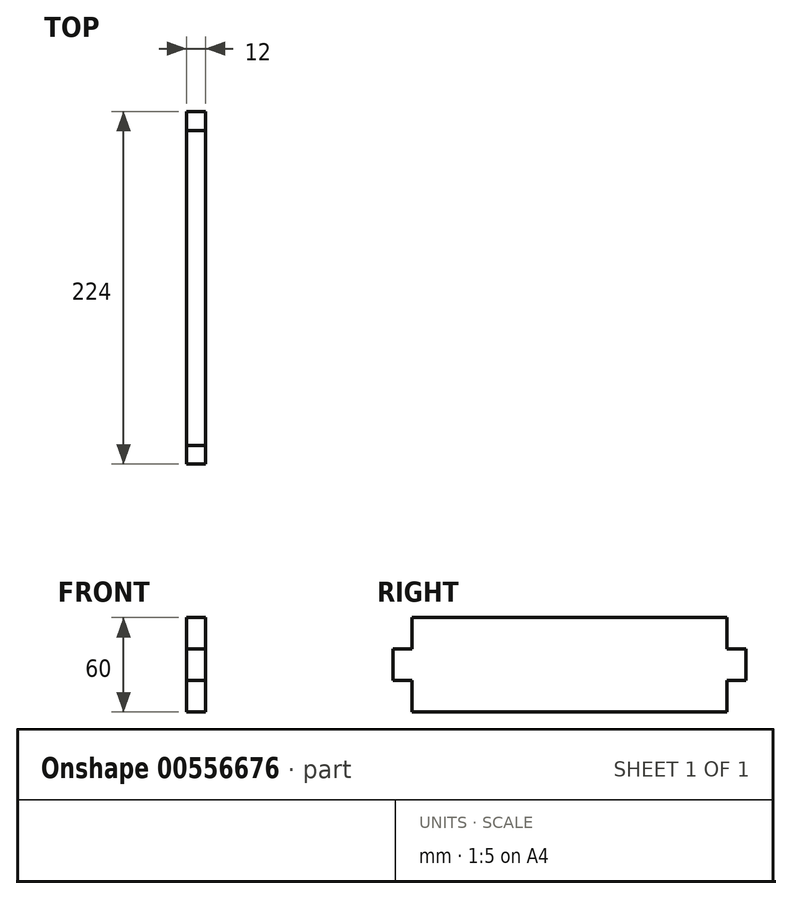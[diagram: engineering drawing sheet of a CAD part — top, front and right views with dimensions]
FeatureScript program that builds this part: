
annotation { "Feature Type Name" : "Feature", "Feature Type Description" : "" }
export const myFeature = defineFeature(function(context is Context, id is Id, definition is map)
    precondition{}
    {
        {
            var Q0;
            Q0=qCreatedBy(makeId("Right.planeOp"),FACE);
            var sketch = newSketch(context, id + "F0", { "sketchPlane" : qUnion([Q0])});
            skLineSegment(sketch, "E0", {"start": v(0, 0) * mm, "end": v(0, 20) * mm});
            skLineSegment(sketch, "E1", {"start": v(0, 20) * mm, "end": v(-12, 20) * mm});
            skLineSegment(sketch, "E2", {"start": v(-12, 20) * mm, "end": v(-12, 40) * mm});
            skLineSegment(sketch, "E3", {"start": v(-12, 40) * mm, "end": v(0, 40) * mm});
            skLineSegment(sketch, "E4", {"start": v(0, 40) * mm, "end": v(0, 60) * mm});
            skLineSegment(sketch, "E5", {"start": v(0, 60) * mm, "end": v(100, 60) * mm});
            skLineSegment(sketch, "E6", {"start": v(100, 60) * mm, "end": v(100, 0) * mm, "construction": true});
            skLineSegment(sketch, "E7", {"start": v(100, 0) * mm, "end": v(0, 0) * mm});
            skLineSegment(sketch, "E8.MirrorCS", {"start": v(200, 20) * mm, "end": v(212, 20) * mm});
            skLineSegment(sketch, "E9.MirrorCS", {"start": v(212, 20) * mm, "end": v(212, 40) * mm});
            skLineSegment(sketch, "E10.MirrorCS", {"start": v(200, 0) * mm, "end": v(200, 20) * mm});
            skLineSegment(sketch, "E11.MirrorCS", {"start": v(200, 60) * mm, "end": v(100, 60) * mm});
            skLineSegment(sketch, "E12.MirrorCS", {"start": v(200, 40) * mm, "end": v(200, 60) * mm});
            skLineSegment(sketch, "E13.MirrorCS", {"start": v(212, 40) * mm, "end": v(200, 40) * mm});
            skLineSegment(sketch, "E14.MirrorCS", {"start": v(100, 0) * mm, "end": v(200, 0) * mm});
            skSolve(sketch);
        }
        {
            var Q0;
            Q0=makeQuery(id+"F0.imprint","IMPRINT",FACE,{"disambiguationData":[TD([[makeQuery(id+"F0.imprint","IMPRINT",EDGE,{"derivedFrom":sQuery(id+"F0.wireOp",EDGE,"E0")}),-1.0]])]});
            extrude(context, id + "F1", {"entities" : qUnion([Q0]), "endBound" : BoundingType.SYMMETRIC, "depth" : 12 * mm, "offsetDistance" : 25 * mm});
        }
    });
